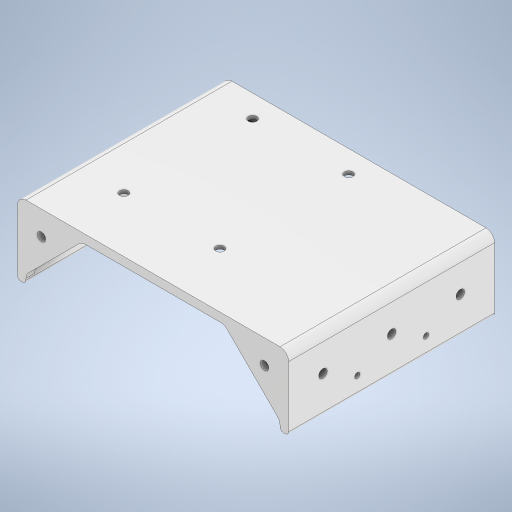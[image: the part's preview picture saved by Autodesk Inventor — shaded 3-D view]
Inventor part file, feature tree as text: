
AUTODESK INVENTOR PART (.ipt)
format: ipt  version: 2024.3 (Build 283343000, 343)  size: 425,984 bytes
history: native  units: mm
features: sketch x9, extrude x7, fillet x3, hole x2, other x1, projected_geometry x1
ambient origin geometry x8: Origin, YZ Plane, XZ Plane, XY Plane, X Axis, Y Axis, Z Axis, Center Point
bodies: Body1 (feature_tree)
feature tree (23):
  other  "ソリッド1"
  extrude  "押し出し1"  Depth=158.0mm
  extrude  "押し出し3"  Depth=250.0mm
  extrude  "押し出し4"  Depth=5.0mm
  hole  "穴2"  [1 undecoded]
  extrude  "押し出し5"  Depth=50.0mm
  extrude  "押し出し6"  Depth=50.0mm
  fillet  "フィレット4"  Radius=30.0mm
  fillet  "フィレット6"  Radius=5.0mm
  extrude  "押し出し8"  Depth=50.0mm
  fillet  "フィレット7"  Radius=50.0mm
  extrude  "押し出し9"  Depth=30.0mm
  hole  "穴3"  [1 undecoded]
  sketch  "スケッチ1"
  sketch  "スケッチ5"
  sketch  "スケッチ6"
  sketch  "スケッチ7"
  sketch  "スケッチ8"
  sketch  "スケッチ9"
  sketch  "スケッチ12"
  projected_geometry  "投影ループ1"
  sketch  "スケッチ13"
  sketch  "スケッチ14"
note: 2 required parameter values undecoded (feature->parameter linkage not recoverable at this tier; creation-order binding heuristic only, values carry confidence <= 0.55)
